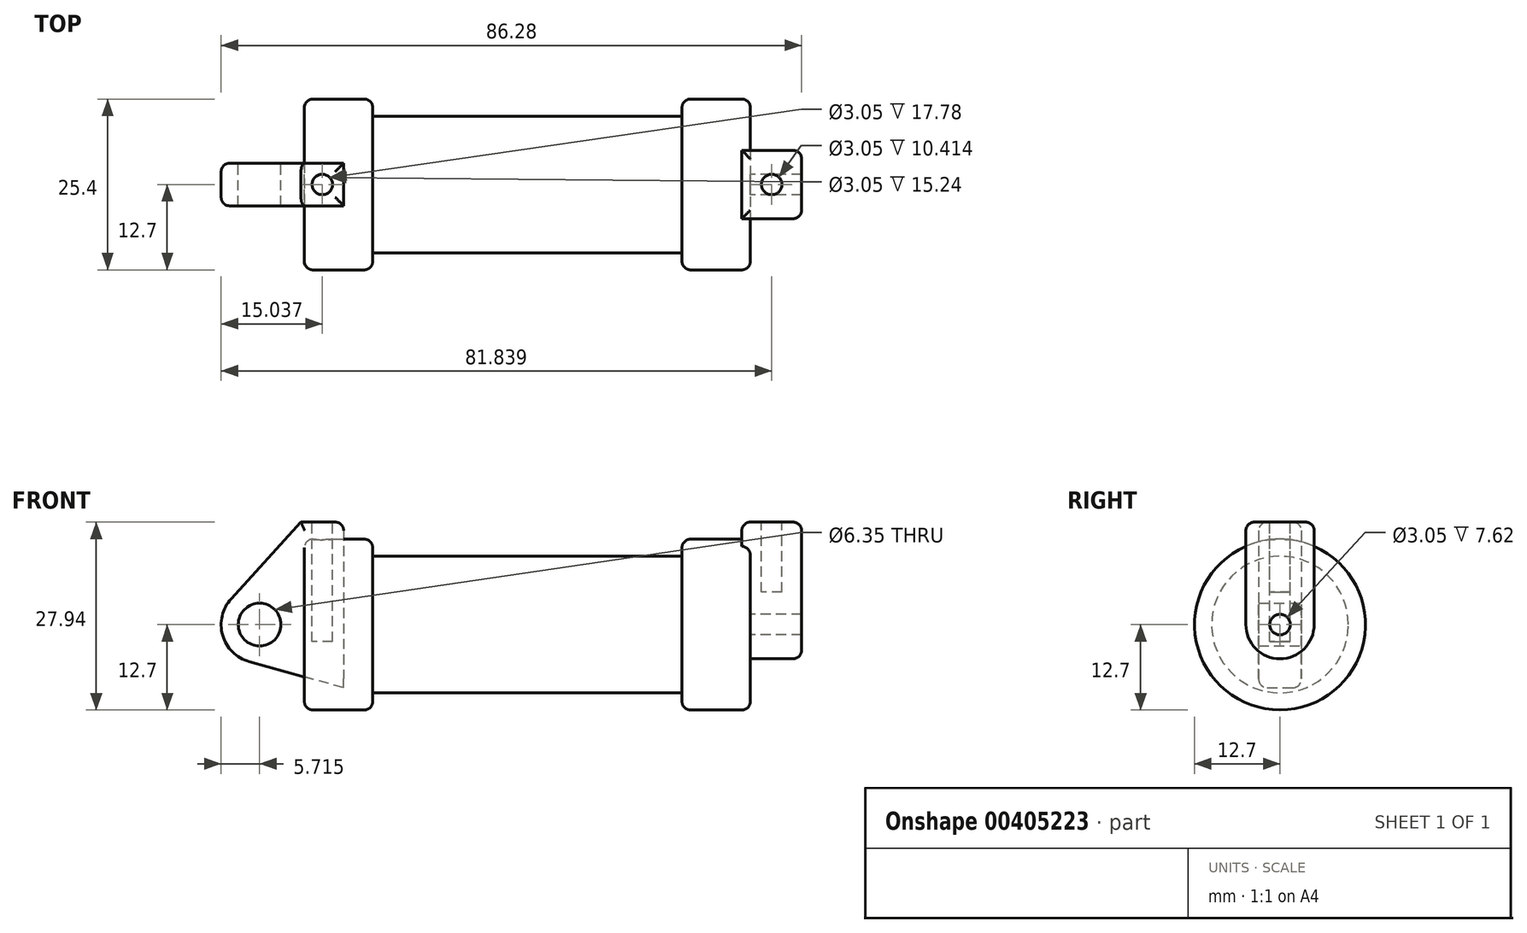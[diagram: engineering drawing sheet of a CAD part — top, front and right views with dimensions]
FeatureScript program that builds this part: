
annotation { "Feature Type Name" : "Feature", "Feature Type Description" : "" }
export const myFeature = defineFeature(function(context is Context, id is Id, definition is map)
    precondition{}
    {
        {
            var Q0;
            Q0=qCreatedBy(makeId("Front.planeOp"),FACE);
            var sketch = newSketch(context, id + "F0", { "sketchPlane" : qUnion([Q0])});
            skLineSegment(sketch, "E0", {"start": v(0, 0) * mm, "end": v(0, 12.7) * mm});
            skLineSegment(sketch, "E1", {"start": v(0, 12.7) * mm, "end": v(10.16, 12.7) * mm});
            skLineSegment(sketch, "E2", {"start": v(10.16, 12.7) * mm, "end": v(10.16, 10.16) * mm});
            skLineSegment(sketch, "E3", {"start": v(10.16, 10.16) * mm, "end": v(56.13, 10.16) * mm});
            skLineSegment(sketch, "E4", {"start": v(56.13, 10.16) * mm, "end": v(56.13, 12.7) * mm});
            skLineSegment(sketch, "E5", {"start": v(56.13, 12.7) * mm, "end": v(66.3, 12.7) * mm});
            skLineSegment(sketch, "E6", {"start": v(66.3, 12.7) * mm, "end": v(66.3, 0) * mm});
            skLineSegment(sketch, "E7", {"start": v(66.3, 0) * mm, "end": v(0, 0) * mm});
            skLineSegment(sketch, "E8", {"start": v(5.84, 15.24) * mm, "end": v(-0.5, 15.24) * mm});
            skLineSegment(sketch, "E9", {"start": v(-0.5, 15.24) * mm, "end": v(-10.88, 3.85) * mm});
            skLineSegment(sketch, "E10", {"start": v(0, 0) * mm, "end": v(-6.65, 0) * mm});
            skCircle(sketch, "E11", {"center": v(-6.65, 0) * mm, "radius": 5.72 * mm});
            skCircle(sketch, "E12", {"center": v(-6.65, 0) * mm, "radius": 3.18 * mm});
            skLineSegment(sketch, "E13", {"start": v(5.84, 15.24) * mm, "end": v(5.84, -9.4) * mm});
            skLineSegment(sketch, "E14", {"start": v(5.84, -9.4) * mm, "end": v(-8.18, -5.5) * mm});
            skSolve(sketch);
        }
        {
            var Q0;
            {var subQ0=sQuery(id+"F0.wireOp",EDGE,"E2");Q0=makeQuery(id+"F0.imprint","IMPRINT",FACE,{"disambiguationData":[TD([[makeQuery(id+"F0.imprint","IMPRINT",EDGE,{"derivedFrom":subQ0}),-1.0]])]});}
            var Q1;
            {var subQ0=sQuery(id+"F0.wireOp",EDGE,"E0");Q1=makeQuery(id+"F0.imprint","IMPRINT",FACE,{"disambiguationData":[TD([[makeQuery(id+"F0.imprint","IMPRINT",EDGE,{"derivedFrom":subQ0}),-1.0]])]});}
            var Q2;
            Q2=sQuery(id+"F0.wireOp",EDGE,"E7");
            revolve(context, id + "F1", {"entities" : qUnion([Q0, Q1]), "axis" : qUnion([Q2]), "revolveType" : RevolveType.FULL});
        }
        {
            var Q0;
            {var subQ0=sQuery(id+"F0.wireOp",EDGE,"E14");Q0=makeQuery(id+"F0.imprint","IMPRINT",FACE,{"disambiguationData":[TD([[makeQuery(id+"F0.imprint","IMPRINT",EDGE,{"derivedFrom":subQ0}),-1.0]])]});}
            var Q1;
            {var subQ5=sQuery(id+"F0.wireOp",EDGE,"E12");Q1=makeQuery(id+"F0.imprint","IMPRINT",FACE,{"disambiguationData":[TD([[makeQuery(id+"F0.imprint","IMPRINT",EDGE,{"derivedFrom":subQ5}),-1.0]])]});}
            var Q2;
            {var subQ1=sQuery(id+"F0.wireOp",EDGE,"E0");Q2=makeQuery(id+"F0.imprint","IMPRINT",FACE,{"disambiguationData":[TD([[makeQuery(id+"F0.imprint","IMPRINT",EDGE,{"derivedFrom":subQ1}),1.0]])]});}
            var Q3;
            {var subQ0=sQuery(id+"F0.wireOp",EDGE,"E0");Q3=makeQuery(id+"F0.imprint","IMPRINT",FACE,{"disambiguationData":[TD([[makeQuery(id+"F0.imprint","IMPRINT",EDGE,{"derivedFrom":subQ0}),-1.0]])]});}
            extrude(context, id + "F2", {"entities" : qUnion([Q0, Q1, Q2, Q3]), "endBound" : BoundingType.SYMMETRIC, "depth" : 6.35 * mm});
        }
        {
            var Q0;
            Q0=makeQuery(id+"F1.opRevolve","SWEPT_FACE",FACE,{"disambiguationData":[OSD([sQuery(id+"F0.wireOp",EDGE,"E6")])]});
            var sketch = newSketch(context, id + "F3", { "sketchPlane" : qUnion([Q0])});
            skCircle(sketch, "E15", {"center": v(0, 0) * mm, "radius": 1.52 * mm});
            skCircle(sketch, "E16", {"center": v(0, 0) * mm, "radius": 5.08 * mm});
            skLineSegment(sketch, "E17", {"start": v(-5.08, 15.24) * mm, "end": v(5.08, 15.24) * mm});
            skLineSegment(sketch, "E18", {"start": v(5.08, 15.24) * mm, "end": v(5.08, 0) * mm});
            skLineSegment(sketch, "E19", {"start": v(-5.08, 15.24) * mm, "end": v(-5.08, 0) * mm});
            skSolve(sketch);
        }
        {
            var Q0;
            {var subQ0=sQuery(id+"F3.wireOp",EDGE,"E17");Q0=makeQuery(id+"F3.imprint","IMPRINT",FACE,{"disambiguationData":[TD([[makeQuery(id+"F3.imprint","IMPRINT",EDGE,{"derivedFrom":subQ0}),-1.0]])]});}
            var Q1;
            {var subQ0=sQuery(id+"F3.wireOp",EDGE,"E18");var subQ1=sQuery(id+"F3.wireOp",EDGE,"E16");var subQ2=makeQuery(id+"F3.imprint","INTERSECT",VERTEX,{"derivedFrom":[subQ1,subQ0]});Q1=makeQuery(id+"F3.imprint","IMPRINT",FACE,{"disambiguationData":[TD([[makeQuery(id+"F3.imprint","IMPRINT",EDGE,{"disambiguationData":[TD([[subQ2,-1.0]])],"derivedFrom":subQ1}),-1.0]])]});}
            var Q2;
            Q2=makeQuery(id+"F3.imprint","IMPRINT",FACE,{"disambiguationData":[TD([[makeQuery(id+"F3.imprint","IMPRINT",EDGE,{"derivedFrom":sQuery(id+"F3.wireOp",EDGE,"E15")}),-1.0]])]});
            extrude(context, id + "F4", {"entities" : qUnion([Q0, Q1, Q2]), "operationType" : NewBodyOperationType.ADD, "depth" : 7.62 * mm});
        }
        {
            var Q0;
            {var subQ0=sQuery(id+"F3.wireOp",EDGE,"E17");Q0=makeQuery(id+"F3.imprint","IMPRINT",FACE,{"disambiguationData":[TD([[makeQuery(id+"F3.imprint","IMPRINT",EDGE,{"derivedFrom":subQ0}),-1.0]])]});}
            var Q1;
            {var subQ0=sQuery(id+"F3.wireOp",EDGE,"E18");var subQ1=sQuery(id+"F3.wireOp",EDGE,"E16");var subQ2=makeQuery(id+"F3.imprint","INTERSECT",VERTEX,{"derivedFrom":[subQ1,subQ0]});Q1=makeQuery(id+"F3.imprint","IMPRINT",FACE,{"disambiguationData":[TD([[makeQuery(id+"F3.imprint","IMPRINT",EDGE,{"disambiguationData":[TD([[subQ2,-1.0]])],"derivedFrom":subQ1}),-1.0]])]});}
            var Q2;
            Q2=makeQuery(id+"F3.imprint","IMPRINT",FACE,{"disambiguationData":[TD([[makeQuery(id+"F3.imprint","IMPRINT",EDGE,{"derivedFrom":sQuery(id+"F3.wireOp",EDGE,"E15")}),-1.0]])]});
            extrude(context, id + "F5", {"entities" : qUnion([Q0, Q1, Q2]), "operationType" : NewBodyOperationType.ADD, "oppositeDirection" : true, "depth" : 1.27 * mm});
        }
        {
            var Q0;
            {var subQ0=sQuery(id+"F3.wireOp",EDGE,"E17");Q0=makeQuery(id+"F5.boolean.opBoolean","MERGE",FACE,{"derivedFrom":[makeQuery(id+"F4.opExtrude","SWEPT_FACE",FACE,{"disambiguationData":[OSD([subQ0])]}),makeQuery(id+"F5.opExtrude","SWEPT_FACE",FACE,{"disambiguationData":[OSD([subQ0])]})]});}
            var sketch = newSketch(context, id + "F6", { "sketchPlane" : qUnion([Q0])});
            skLineSegment(sketch, "E20", {"start": v(73.91, 0) * mm, "end": v(-6.46, 0) * mm, "construction": true});
            skPoint(sketch, "E20.endSnap0", {"position": v(73.91, 0) * mm});
            skLineSegment(sketch, "E21", {"start": v(69.47, 5.08) * mm, "end": v(69.47, -5.08) * mm, "construction": true});
            skCircle(sketch, "E22", {"center": v(69.47, 0) * mm, "radius": 1.52 * mm});
            skSolve(sketch);
        }
        {
            var Q0;
            Q0=makeQuery(id+"F6.imprint","IMPRINT",FACE,{"disambiguationData":[TD([[makeQuery(id+"F6.imprint","IMPRINT",EDGE,{"derivedFrom":sQuery(id+"F6.wireOp",EDGE,"E22")}),1.0]])]});
            var Q1;
            Q1=sQuery(id+"F6.wireOp",EDGE,"E22");
            extrude(context, id + "F7", {"entities" : qUnion([Q0]), "operationType" : NewBodyOperationType.REMOVE, "surfaceEntities" : qUnion([Q1]), "oppositeDirection" : true, "depth" : 10.4 * mm});
        }
        {
            var Q0;
            Q0=makeQuery(id+"F2.opExtrude","SWEPT_FACE",FACE,{"disambiguationData":[OSD([sQuery(id+"F0.wireOp",EDGE,"E8")])]});
            var sketch = newSketch(context, id + "F8", { "sketchPlane" : qUnion([Q0])});
            skLineSegment(sketch, "E23", {"start": v(2.67, -3.18) * mm, "end": v(2.67, 3.18) * mm, "construction": true});
            skCircle(sketch, "E24", {"center": v(2.67, 0) * mm, "radius": 1.52 * mm});
            skSolve(sketch);
        }
        {
            var Q0;
            Q0=makeQuery(id+"F8.imprint","IMPRINT",FACE,{"disambiguationData":[TD([[makeQuery(id+"F8.imprint","IMPRINT",EDGE,{"derivedFrom":sQuery(id+"F8.wireOp",EDGE,"E24")}),1.0]])]});
            extrude(context, id + "F9", {"entities" : qUnion([Q0]), "operationType" : NewBodyOperationType.REMOVE, "oppositeDirection" : true, "depth" : 17.78 * mm});
        }
        {
            var Q0;
            Q0=makeQuery(id+"F2.opExtrude","CAP_EDGE",EDGE,{"disambiguationData":[OSD([sQuery(id+"F0.wireOp",EDGE,"E8")])],"isStart":true});
            var Q1;
            Q1=makeQuery(id+"F2.opExtrude","CAP_EDGE",EDGE,{"disambiguationData":[OSD([sQuery(id+"F0.wireOp",EDGE,"E8")])],"isStart":false});
            var Q2;
            Q2=makeQuery(id+"F2.opExtrude","SWEPT_EDGE",EDGE,{"disambiguationData":[OSD([sQuery(id+"F0.wireOp",EDGE,"E8"),sQuery(id+"F0.wireOp",EDGE,"E13")])]});
            var Q3;
            Q3=makeQuery(id+"F2.opExtrude","CAP_EDGE",EDGE,{"disambiguationData":[OSD([sQuery(id+"F0.wireOp",EDGE,"E9")])],"isStart":false});
            var Q4;
            Q4=makeQuery(id+"F2.opExtrude","CAP_EDGE",EDGE,{"disambiguationData":[OSD([sQuery(id+"F0.wireOp",EDGE,"E9")])],"isStart":true});
            var Q5;
            Q5=makeQuery(id+"F2.opExtrude","CAP_EDGE",EDGE,{"disambiguationData":[OSD([sQuery(id+"F0.wireOp",EDGE,"E11")])],"isStart":true});
            var Q6;
            Q6=makeQuery(id+"F1.opRevolve","SWEPT_EDGE",EDGE,{"disambiguationData":[OSD([sQuery(id+"F0.wireOp",EDGE,"E0"),sQuery(id+"F0.wireOp",EDGE,"E1")])]});
            var Q7;
            Q7=makeQuery(id+"F1.opRevolve","SWEPT_EDGE",EDGE,{"disambiguationData":[OSD([sQuery(id+"F0.wireOp",EDGE,"E1"),sQuery(id+"F0.wireOp",EDGE,"E2")])]});
            var Q8;
            Q8=makeQuery(id+"F1.opRevolve","SWEPT_EDGE",EDGE,{"disambiguationData":[OSD([sQuery(id+"F0.wireOp",EDGE,"E4"),sQuery(id+"F0.wireOp",EDGE,"E5")])]});
            var Q9;
            {var subQ0=sQuery(id+"F0.wireOp",EDGE,"E5");var subQ1=sQuery(id+"F0.wireOp",EDGE,"E6");Q9=makeQuery(id+"F4.boolean.opBoolean","SPLIT",EDGE,{"disambiguationData":[topologyDisambiguationEdgeConnected([makeQuery(id+"F1.opRevolve","SWEPT_FACE",FACE,{"disambiguationData":[OSD([subQ1])]})])],"derivedFrom":makeQuery(id+"F1.opRevolve","SWEPT_EDGE",EDGE,{"disambiguationData":[OSD([subQ0,subQ1])]})});}
            var Q10;
            {var subQ0=sQuery(id+"F3.wireOp",EDGE,"E19");var subQ1=sQuery(id+"F3.wireOp",EDGE,"E17");Q10=makeQuery(id+"F5.boolean.opBoolean","MERGE",EDGE,{"derivedFrom":[makeQuery(id+"F4.opExtrude","SWEPT_EDGE",EDGE,{"disambiguationData":[OSD([subQ1,subQ0])]}),makeQuery(id+"F5.opExtrude","SWEPT_EDGE",EDGE,{"disambiguationData":[OSD([subQ1,subQ0])]})]});}
            var Q11;
            Q11=makeQuery(id+"F5.opExtrude","CAP_EDGE",EDGE,{"disambiguationData":[OSD([sQuery(id+"F3.wireOp",EDGE,"E17")])],"isStart":false});
            var Q12;
            Q12=makeQuery(id+"F4.opExtrude","CAP_EDGE",EDGE,{"disambiguationData":[OSD([sQuery(id+"F3.wireOp",EDGE,"E17")])],"isStart":false});
            var Q13;
            {var subQ0=sQuery(id+"F3.wireOp",EDGE,"E18");var subQ1=sQuery(id+"F3.wireOp",EDGE,"E17");Q13=makeQuery(id+"F5.boolean.opBoolean","MERGE",EDGE,{"derivedFrom":[makeQuery(id+"F4.opExtrude","SWEPT_EDGE",EDGE,{"disambiguationData":[OSD([subQ1,subQ0])]}),makeQuery(id+"F5.opExtrude","SWEPT_EDGE",EDGE,{"disambiguationData":[OSD([subQ1,subQ0])]})]});}
            var Q14;
            Q14=makeQuery(id+"F4.opExtrude","CAP_EDGE",EDGE,{"disambiguationData":[OSD([sQuery(id+"F3.wireOp",EDGE,"E19")])],"isStart":false});
            fillet(context, id + "F10", {"entities" : qUnion([Q0, Q1, Q2, Q3, Q4, Q5, Q6, Q7, Q8, Q9, Q10, Q11, Q12, Q13, Q14]), "radius" : 1.27 * mm, "tangentPropagation" : true, "allowEdgeOverflow" : false});
        }
    });
